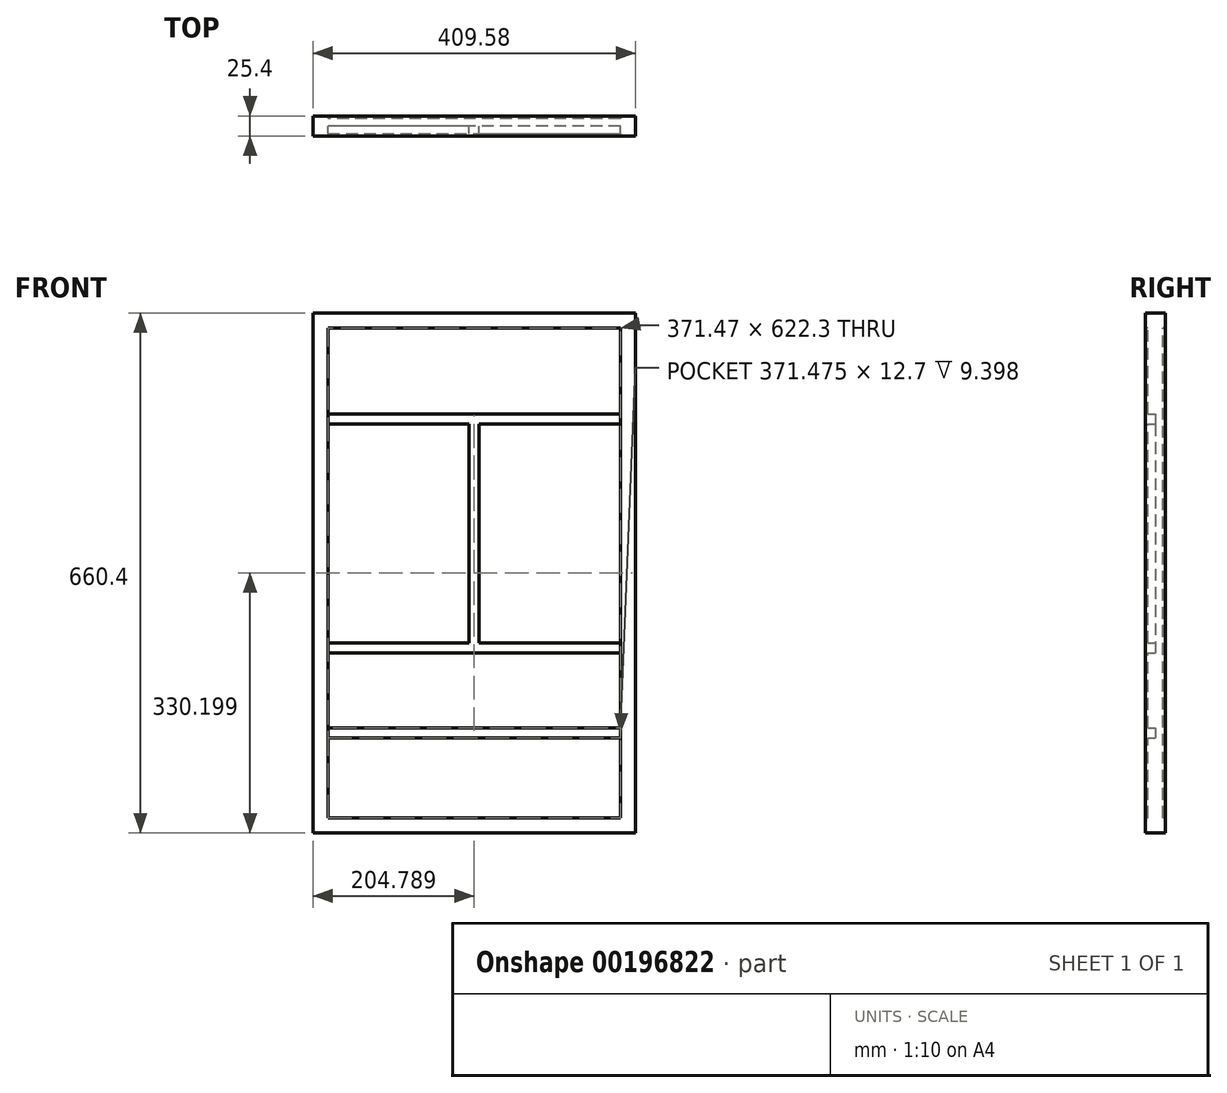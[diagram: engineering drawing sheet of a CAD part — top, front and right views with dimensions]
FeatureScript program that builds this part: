
annotation { "Feature Type Name" : "Feature", "Feature Type Description" : "" }
export const myFeature = defineFeature(function(context is Context, id is Id, definition is map)
    precondition{}
    {
        {
            var Q0;
            Q0=qCreatedBy(makeId("Front.planeOp"),FACE);
            var sketch = newSketch(context, id + "F0", { "sketchPlane" : qUnion([Q0])});
            skLineSegment(sketch, "E0.right", {"start": v(634.52, 506.05) * mm, "end": v(634.52, -116.25) * mm});
            skLineSegment(sketch, "E1.trimOffspring", {"start": v(263.04, 506.05) * mm, "end": v(634.52, 506.05) * mm});
            skPoint(sketch, "E0.left.start.orphan", {"position": v(-231.42, 527.58) * mm});
            skPoint(sketch, "E2.top.end.orphan", {"position": v(1181.04, -116.25) * mm});
            skLineSegment(sketch, "E3.top", {"start": v(244, -135.3) * mm, "end": v(653.57, -135.3) * mm});
            skLineSegment(sketch, "E4", {"start": v(634.52, -116.25) * mm, "end": v(263.04, -116.25) * mm});
            skLineSegment(sketch, "E5", {"start": v(244, 525.1) * mm, "end": v(244, -135.3) * mm});
            skLineSegment(sketch, "E6", {"start": v(244, 525.1) * mm, "end": v(653.57, 525.1) * mm});
            skLineSegment(sketch, "E7", {"start": v(653.57, -135.3) * mm, "end": v(653.57, 525.1) * mm});
            skLineSegment(sketch, "E8", {"start": v(634.52, 506.05) * mm, "end": v(653.57, 525.1) * mm});
            skLineSegment(sketch, "E9", {"start": v(263.04, 506.05) * mm, "end": v(244, 525.1) * mm});
            skLineSegment(sketch, "E10", {"start": v(263.04, -116.25) * mm, "end": v(244, -135.3) * mm});
            skLineSegment(sketch, "E11", {"start": v(634.52, -116.25) * mm, "end": v(653.57, -135.3) * mm});
            skLineSegment(sketch, "E12", {"start": v(263.04, 506.05) * mm, "end": v(263.04, -116.25) * mm});
            skSolve(sketch);
        }
        {
            var Q0;
            Q0=makeQuery(id+"F0.imprint","IMPRINT",FACE,{"disambiguationData":[TD([[makeQuery(id+"F0.imprint","IMPRINT",EDGE,{"derivedFrom":sQuery(id+"F0.wireOp",EDGE,"E0.bottom")}),-1.0]])]});
            var Q1;
            {var subQ0=sQuery(id+"F0.wireOp",EDGE,"E0.left");Q1=makeQuery(id+"F0.imprint","IMPRINT",FACE,{"disambiguationData":[TD([[makeQuery(id+"F0.imprint","IMPRINT",EDGE,{"derivedFrom":subQ0}),1.0]])]});}
            var Q2;
            Q2=makeQuery(id+"F0.imprint","IMPRINT",FACE,{"disambiguationData":[TD([[makeQuery(id+"F0.imprint","IMPRINT",EDGE,{"derivedFrom":sQuery(id+"F0.wireOp",EDGE,"E2.bottom")}),-1.0]])]});
            var Q3;
            Q3=makeQuery(id+"F0.imprint","IMPRINT",FACE,{"disambiguationData":[TD([[makeQuery(id+"F0.imprint","IMPRINT",EDGE,{"derivedFrom":sQuery(id+"F0.wireOp",EDGE,"E1.trimOffspring")}),1.0]])]});
            var Q4;
            Q4=makeQuery(id+"F0.imprint","IMPRINT",FACE,{"disambiguationData":[TD([[makeQuery(id+"F0.imprint","IMPRINT",EDGE,{"derivedFrom":sQuery(id+"F0.wireOp",EDGE,"8p2t2OPa-LCOw-EM91-35Oi-yHNuIQBoYJnY.right")}),-1.0]])]});
            var Q5;
            Q5=makeQuery(id+"F0.imprint","IMPRINT",FACE,{"disambiguationData":[TD([[makeQuery(id+"F0.imprint","IMPRINT",EDGE,{"derivedFrom":sQuery(id+"F0.wireOp",EDGE,"E0.right")}),1.0]])]});
            var Q6;
            Q6=makeQuery(id+"F0.imprint","IMPRINT",FACE,{"disambiguationData":[TD([[makeQuery(id+"F0.imprint","IMPRINT",EDGE,{"derivedFrom":sQuery(id+"F0.wireOp",EDGE,"E3.top")}),1.0]])]});
            var Q7;
            Q7=makeQuery(id+"F0.imprint","IMPRINT",FACE,{"disambiguationData":[TD([[makeQuery(id+"F0.imprint","IMPRINT",EDGE,{"derivedFrom":sQuery(id+"F0.wireOp",EDGE,"E5")}),1.0]])]});
            extrude(context, id + "F1", {"entities" : qUnion([Q0, Q1, Q2, Q3, Q4, Q5, Q6, Q7]), "oppositeDirection" : true, "depth" : 12.7 * mm, "hasSecondDirection" : true, "secondDirectionOppositeDirection" : true, "secondDirectionDepth" : -12.7 * mm, "offsetDistance" : 25.4 * mm});
        }
        {
            var Q0;
            Q0=makeQuery(id+"F0.imprint","IMPRINT",FACE,{"disambiguationData":[TD([[makeQuery(id+"F0.imprint","IMPRINT",EDGE,{"derivedFrom":sQuery(id+"F0.wireOp",EDGE,"E0.right")}),1.0]])]});
            var Q1;
            Q1=makeQuery(id+"F0.imprint","IMPRINT",FACE,{"disambiguationData":[TD([[makeQuery(id+"F0.imprint","IMPRINT",EDGE,{"derivedFrom":sQuery(id+"F0.wireOp",EDGE,"E1.trimOffspring")}),1.0]])]});
            var Q2;
            Q2=makeQuery(id+"F0.imprint","IMPRINT",FACE,{"disambiguationData":[TD([[makeQuery(id+"F0.imprint","IMPRINT",EDGE,{"derivedFrom":sQuery(id+"F0.wireOp",EDGE,"E3.top")}),1.0]])]});
            var Q3;
            Q3=makeQuery(id+"F0.imprint","IMPRINT",FACE,{"disambiguationData":[TD([[makeQuery(id+"F0.imprint","IMPRINT",EDGE,{"derivedFrom":sQuery(id+"F0.wireOp",EDGE,"E0.right")}),-1.0]])]});
            var Q4;
            Q4=makeQuery(id+"F0.imprint","IMPRINT",FACE,{"disambiguationData":[TD([[makeQuery(id+"F0.imprint","IMPRINT",EDGE,{"derivedFrom":sQuery(id+"F0.wireOp",EDGE,"gC7cCnke-s9s4-gMFU-noRS-npdH3P1wzTm0")}),1.0]])]});
            var Q5;
            Q5=makeQuery(id+"F0.imprint","IMPRINT",FACE,{"disambiguationData":[TD([[makeQuery(id+"F0.imprint","IMPRINT",EDGE,{"derivedFrom":sQuery(id+"F0.wireOp",EDGE,"E5")}),1.0]])]});
            extrude(context, id + "F2", {"entities" : qUnion([Q0, Q1, Q2, Q3, Q4, Q5]), "operationType" : NewBodyOperationType.ADD, "oppositeDirection" : true, "depth" : 9.4 * mm, "offsetDistance" : 25.4 * mm, "hasSecondDirection" : true, "secondDirectionOppositeDirection" : true, "secondDirectionDepth" : -9.4 * mm});
        }
        {
            var Q0;
            Q0=makeQuery(id+"F0.imprint","IMPRINT",FACE,{"disambiguationData":[TD([[makeQuery(id+"F0.imprint","IMPRINT",EDGE,{"derivedFrom":sQuery(id+"F0.wireOp",EDGE,"E0.right")}),-1.0]])]});
            var sketch = newSketch(context, id + "F3", { "sketchPlane" : qUnion([Q0])});
            skLineSegment(sketch, "E13.left", {"start": v(455.13, 384.13) * mm, "end": v(455.13, 106) * mm});
            skLineSegment(sketch, "E13.right", {"start": v(442.43, 384.13) * mm, "end": v(442.43, 106) * mm});
            skLineSegment(sketch, "E14.bottom", {"start": v(634.52, -14.65) * mm, "end": v(263.04, -14.65) * mm});
            skLineSegment(sketch, "E14.right", {"start": v(263.04, -14.65) * mm, "end": v(263.04, -1.95) * mm});
            skLineSegment(sketch, "E15", {"start": v(634.52, -1.95) * mm, "end": v(634.52, -14.65) * mm});
            skLineSegment(sketch, "E16.bottom", {"start": v(634.52, 384.13) * mm, "end": v(455.13, 384.13) * mm});
            skLineSegment(sketch, "E16.top", {"start": v(634.52, 396.83) * mm, "end": v(263.04, 396.83) * mm});
            skLineSegment(sketch, "E16.left", {"start": v(634.52, 384.13) * mm, "end": v(634.52, 396.83) * mm});
            skLineSegment(sketch, "E16.right", {"start": v(263.04, 384.13) * mm, "end": v(263.04, 396.83) * mm});
            skLineSegment(sketch, "E17.trimOffspring", {"start": v(442.43, 384.13) * mm, "end": v(263.04, 384.13) * mm});
            skLineSegment(sketch, "E18.top", {"start": v(634.52, 106) * mm, "end": v(455.13, 106) * mm});
            skLineSegment(sketch, "E18.left", {"start": v(634.52, 93.3) * mm, "end": v(634.52, 106) * mm});
            skLineSegment(sketch, "E18.right", {"start": v(263.04, 93.3) * mm, "end": v(263.04, 106) * mm});
            skLineSegment(sketch, "E19.trimOffspring", {"start": v(442.43, 106) * mm, "end": v(263.04, 106) * mm});
            skLineSegment(sketch, "E20", {"start": v(263.04, -1.95) * mm, "end": v(634.52, -1.95) * mm});
            skLineSegment(sketch, "E21", {"start": v(634.52, 93.3) * mm, "end": v(263.04, 93.3) * mm});
            skSolve(sketch);
        }
        {
            var Q0;
            Q0 = qSketchRegion(id + "F3", true);
            extrude(context, id + "F4", {"entities" : qUnion([Q0]), "operationType" : NewBodyOperationType.REMOVE, "depth" : 12.7 * mm, "offsetDistance" : 25.4 * mm});
        }
    });
